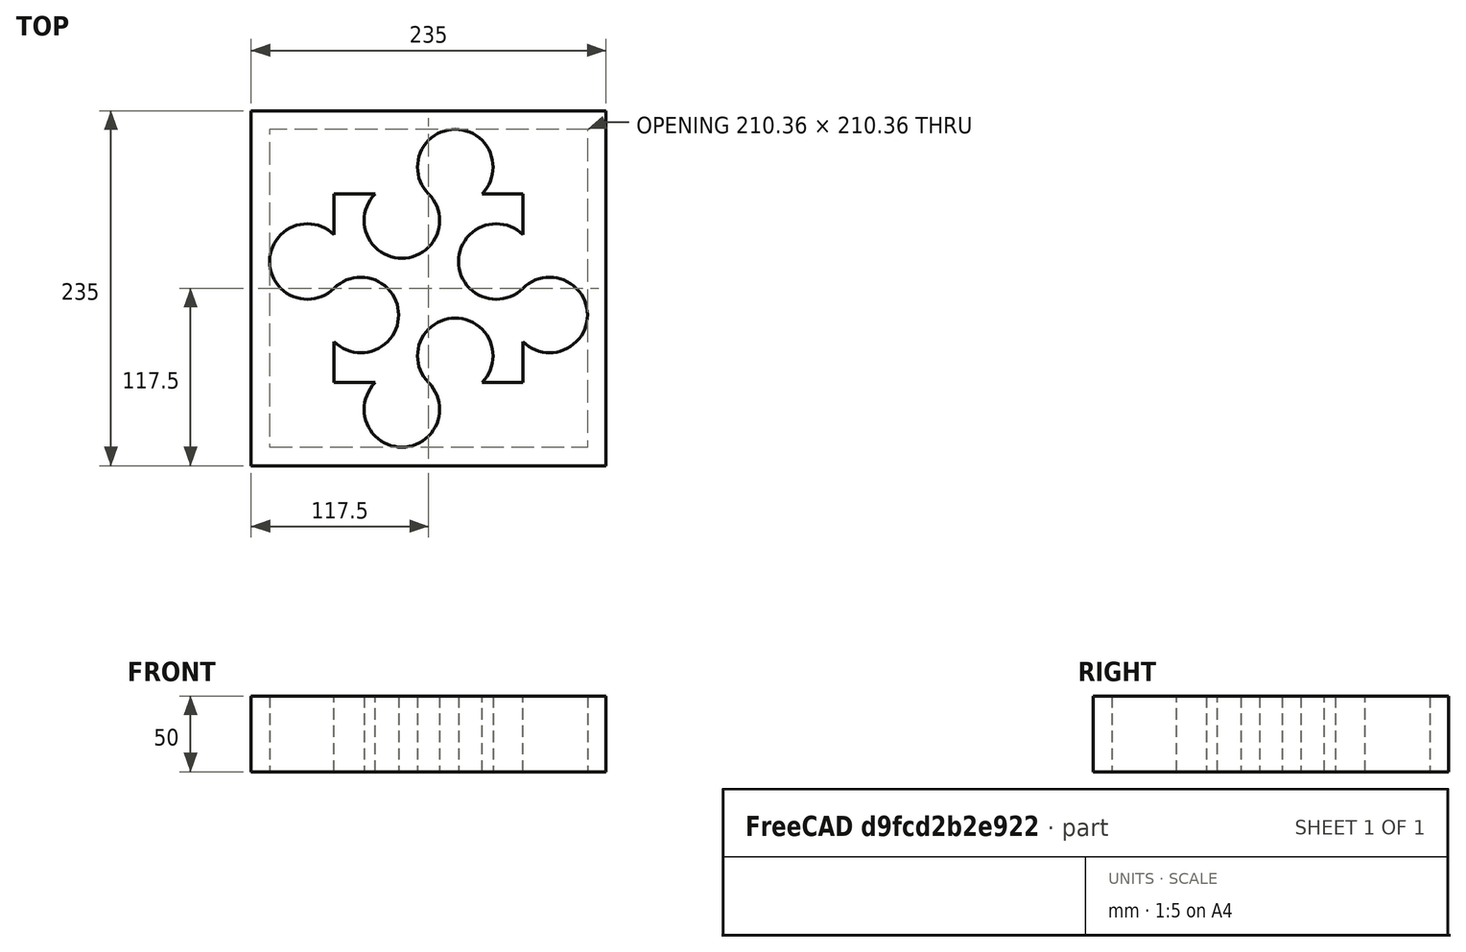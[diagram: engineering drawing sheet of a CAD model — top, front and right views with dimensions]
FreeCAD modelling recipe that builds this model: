
FCSTD DOCUMENT  (FreeCAD 2023.131R26244 +5365 (Git))
Label: Tesselation Mold
License: All rights reserved
LicenseURL: http://en.wikipedia.org/wiki/All_rights_reserved
objects: Sketcher::SketchObject×1, Spreadsheet::Sheet×1, PartDesign::Pad×1, PartDesign::Body×1
note: 6 computed .brp shape members not serialized (recipe doc carries the construction recipe); baked Part::Feature solids carry a one-line shape summary decoded from their .brp

FEATURE [Sketcher::SketchObject] Sketch
  ArcFitTolerance = 1e-06
  AttachmentSupport = -> [XY_Plane]
  ExternalBSplineMaxDegree = 5
  ExternalBSplineTolerance = 0.0001
  FullyConstrained = true
  InternalTolerance = 1e-06
  InvalidShape = false
  MakeInternals = false
  MapMode = 5
  Support = -> [XY_Plane]
  TreeRank = 12
  ValidateShape = true
  expr: Constraints[10] = <<Parameters>>.square_length
  expr: Constraints[12] = <<Parameters>>.circle_radius
  expr: Constraints[71] = <<Parameters>>.square_length
  expr: Constraints[83] = <<Parameters>>.peremeter_length
  sketch-geometry (30):
    g0: LineSegment StartX=62.5 StartY=-62.5 StartZ=0 EndX=62.5 EndY=-35.3553 EndZ=0
    g1: LineSegment StartX=62.5 StartY=62.5 StartZ=0 EndX=35.3553 EndY=62.5 EndZ=0
    g2: LineSegment StartX=-62.5 StartY=62.5 StartZ=0 EndX=-62.5 EndY=35.3554 EndZ=0
    g3: LineSegment StartX=-62.5 StartY=-62.5 StartZ=0 EndX=-35.3553 EndY=-62.5 EndZ=0
    g4: GeomPoint [constr] X=0 Y=0 Z=0
    g5: ArcOfCircle CenterX=-80.1776 CenterY=17.6777 CenterZ=0 NormalX=0 NormalY=0 NormalZ=1 AngleXU=0 Radius=25 StartAngle=0.7854 EndAngle=5.49779
    g6: ArcOfCircle CenterX=-44.8223 CenterY=-17.6776 CenterZ=0 NormalX=0 NormalY=0 NormalZ=1 AngleXU=0 Radius=25 StartAngle=3.92699 EndAngle=8.63938
    g7: GeomPoint [constr] X=-62.5 Y=0 Z=0
    g8: LineSegment [constr] StartX=-44.8223 StartY=-17.6776 StartZ=0 EndX=-80.1776 EndY=17.6777 EndZ=0
    g9: LineSegment StartX=-62.5 StartY=-35.3553 StartZ=0 EndX=-62.5 EndY=-62.5 EndZ=0
    g10: ArcOfCircle CenterX=-17.6777 CenterY=-80.1777 CenterZ=0 NormalX=0 NormalY=0 NormalZ=1 AngleXU=0 Radius=25 StartAngle=2.35619 EndAngle=7.06858
    g11: ArcOfCircle CenterX=17.6777 CenterY=-44.8223 CenterZ=0 NormalX=0 NormalY=0 NormalZ=1 AngleXU=0 Radius=25 StartAngle=5.49779 EndAngle=10.2102
    g12: ArcOfCircle CenterX=80.1777 CenterY=-17.6777 CenterZ=0 NormalX=0 NormalY=0 NormalZ=1 AngleXU=0 Radius=25 StartAngle=3.92699 EndAngle=8.63938
    g13: ArcOfCircle CenterX=44.8223 CenterY=17.6777 CenterZ=0 NormalX=0 NormalY=0 NormalZ=1 AngleXU=0 Radius=25 StartAngle=0.785398 EndAngle=5.49779
    g14: ArcOfCircle CenterX=17.6777 CenterY=80.1777 CenterZ=0 NormalX=0 NormalY=0 NormalZ=1 AngleXU=0 Radius=25 StartAngle=5.49779 EndAngle=10.2102
    g15: ArcOfCircle CenterX=-17.6777 CenterY=44.8223 CenterZ=0 NormalX=0 NormalY=0 NormalZ=1 AngleXU=0 Radius=25 StartAngle=2.35619 EndAngle=7.06859
    g16: GeomPoint [constr] X=0 Y=62.5 Z=0
    g17: LineSegment [constr] StartX=-17.6777 StartY=44.8223 StartZ=0 EndX=17.6777 EndY=80.1777 EndZ=0
    g18: GeomPoint [constr] X=62.5 Y=0 Z=0
    g19: GeomPoint [constr] X=0 Y=-62.5 Z=0
    g20: LineSegment [constr] StartX=44.8223 StartY=17.6777 StartZ=0 EndX=80.1777 EndY=-17.6777 EndZ=0
    g21: LineSegment [constr] StartX=17.6777 StartY=-44.8223 StartZ=0 EndX=-17.6777 EndY=-80.1777 EndZ=0
    g22: LineSegment StartX=-35.3553 StartY=62.5 StartZ=0 EndX=-62.5 EndY=62.5 EndZ=0
    g23: LineSegment StartX=62.5 StartY=35.3553 StartZ=0 EndX=62.5 EndY=62.5 EndZ=0
    g24: LineSegment StartX=35.3553 StartY=-62.5 StartZ=0 EndX=62.5 EndY=-62.5 EndZ=0
    g25: LineSegment StartX=117.5 StartY=-117.5 StartZ=0 EndX=117.5 EndY=117.5 EndZ=0
    g26: LineSegment StartX=117.5 StartY=117.5 StartZ=0 EndX=-117.5 EndY=117.5 EndZ=0
    g27: LineSegment StartX=-117.5 StartY=117.5 StartZ=0 EndX=-117.5 EndY=-117.5 EndZ=0
    g28: LineSegment StartX=-117.5 StartY=-117.5 StartZ=0 EndX=117.5 EndY=-117.5 EndZ=0
    g29: GeomPoint [constr] X=0 Y=0 Z=0
  constraints (84):
    c: Coincident(g23,g1)
    c: Coincident(g22,g2)
    c: Coincident(g9,g3)
    c: Coincident(g24,g0)
    c: Horizontal(g1)
    c: Horizontal(g3)
    c: Vertical(g0)
    c: Vertical(g2)
    c: Symmetric(g22,g0,g4)
    c: Coincident(g4,g-1)
    c: DistanceX(g22,g23) = 125
    c: Equal(g5,g6)
    c: Diameter(g5) = 50
    c: PointOnObject(g7,g5)
    c: PointOnObject(g7,g6)
    c: PointOnObject(g7,g-1)
    c: PointOnObject(g7,g2)
    c: Coincident(g8,g6)
    c: Coincident(g8,g5)
    c: Angle(g-1,g8) = 2.35619
    c: Coincident(g6,g9)
    c: Coincident(g5,g2)
    c: Coincident(g5,g6)
    c: Vertical(g9)
    c: DistanceX(g3,g22) = 0
    c: PointOnObject(g5,g8)
    c: Equal(g5,g15)
    c: Equal(g5,g14)
    c: Equal(g5,g13)
    c: Equal(g5,g12)
    c: Equal(g5,g11)
    c: Equal(g5,g10)
    c: PointOnObject(g16,g15)
    c: PointOnObject(g16,g14)
    c: PointOnObject(g16,g-2)
    c: Coincident(g17,g15)
    c: Coincident(g17,g14)
    c: PointOnObject(g16,g1)
    c: PointOnObject(g18,g13)
    c: PointOnObject(g19,g11)
    c: PointOnObject(g18,g12)
    c: PointOnObject(g18,g-1)
    c: PointOnObject(g19,g10)
    c: PointOnObject(g19,g-2)
    c: Coincident(g20,g13)
    c: Coincident(g20,g12)
    c: Coincident(g21,g11)
    c: Coincident(g21,g10)
    c: PointOnObject(g16,g17)
    c: PointOnObject(g18,g20)
    c: PointOnObject(g19,g21)
    c: PointOnObject(g18,g0)
    c: PointOnObject(g19,g3)
    c: Coincident(g15,g22)
    c: Coincident(g14,g15)
    c: Coincident(g14,g1)
    c: Coincident(g13,g23)
    c: Coincident(g12,g13)
    c: Coincident(g12,g0)
    c: Coincident(g11,g24)
    c: Coincident(g10,g11)
    c: Coincident(g10,g3)
    c: Vertical(g23)
    c: Horizontal(g24)
    c: Horizontal(g22)
    c: DistanceX(g1,g0) = 0
    c: DistanceY(g3,g0) = 0
    c: DistanceY(g1,g2) = 0
    c: Angle(g17,g-2) = 0.785398
    c: Angle(g20,g-1) = 0.785398
    c: Angle(g21,g-2) = 0.785398
    c: DistanceY(g0,g1) = 125
    c: Coincident(g25,g26)
    c: Coincident(g26,g27)
    c: Coincident(g27,g28)
    c: Coincident(g28,g25)
    c: Horizontal(g26)
    c: Horizontal(g28)
    c: Vertical(g25)
    c: Vertical(g27)
    c: Symmetric(g26,g25,g29)
    c: Coincident(g29,g4)
    c: Equal(g26,g25)
    c: DistanceX(g26,g25) = 235
FEATURE [Spreadsheet::Sheet] Spreadsheet  label="Parameters"
  PythonMode = false
  ShowCells = 0
  TreeRank = 10
  cells = A1=Square Length; B1(square_length)=125; A2=Circle Diameter; B2(circle_radius)==square_length / 2.5; A3=Permeter Length; B3(peremeter_length)==square_length + circle_radius * 2 + 10
FEATURE [PartDesign::Pad] Pad
  AddSubType = 0
  AlongSketchNormal = false
  AutoTaperInnerAngle = true
  CheckUpToFaceLimits = true
  ClaimChildren = false
  Direction = (0,0,1)
  Fit = 0
  FitJoin = 0
  InnerFit = 0
  InnerFitJoin = 0
  InvalidShape = false
  Length = 50
  Length2 = 100
  Linearize = true
  NewSolid = false
  Profile = -> Sketch
  Suppress = false
  TaperInnerAngle = 0
  TaperInnerAngleRev = 0
  TreeRank = 13
  Type = 0
  ValidateShape = true
  _ProfileBasedVersion = 1
FEATURE [PartDesign::Body] Body
  AutoGroupSolids = false
  ClaimAllChildren = false
  ExportMode = 0
  Group = -> [Sketch,Pad]
  InvalidShape = false
  Origin = -> Origin
  Tip = -> Pad
  TreeRank = 11
  ValidateShape = true
  _ExportChildren = -> [Pad]
  _GroupVersion = 1
